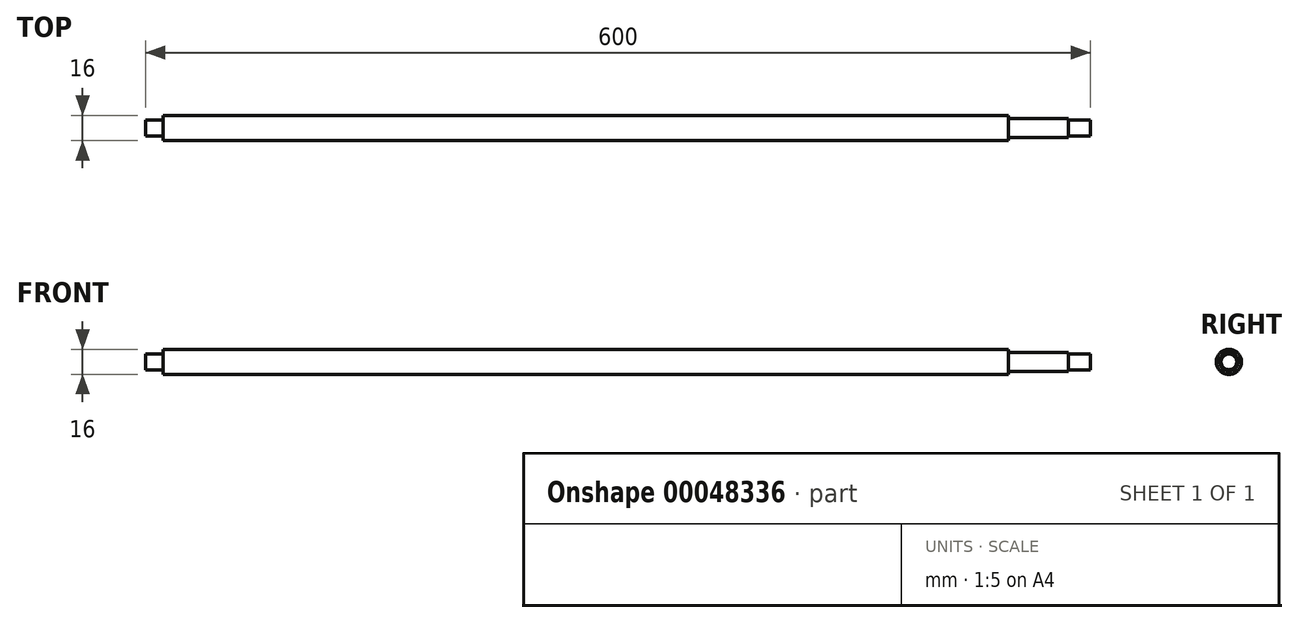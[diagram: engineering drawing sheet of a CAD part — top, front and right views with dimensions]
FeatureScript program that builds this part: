
annotation { "Feature Type Name" : "Feature", "Feature Type Description" : "" }
export const myFeature = defineFeature(function(context is Context, id is Id, definition is map)
    precondition{}
    {
        {
            var Q0;
            Q0=qCreatedBy(makeId("Top.planeOp"),FACE);
            var sketch = newSketch(context, id + "F0", { "sketchPlane" : qUnion([Q0])});
            skLineSegment(sketch, "E0", {"start": v(-350.57, -40.96) * mm, "end": v(249.43, -40.96) * mm});
            skLineSegment(sketch, "E1", {"start": v(-350.57, -40.96) * mm, "end": v(-350.57, -35.96) * mm});
            skLineSegment(sketch, "E2", {"start": v(-350.57, -35.96) * mm, "end": v(-339.57, -35.96) * mm});
            skLineSegment(sketch, "E3", {"start": v(-339.57, -35.96) * mm, "end": v(-339.57, -32.96) * mm});
            skLineSegment(sketch, "E4", {"start": v(-339.57, -32.96) * mm, "end": v(197.43, -32.96) * mm});
            skLineSegment(sketch, "E5", {"start": v(197.43, -32.96) * mm, "end": v(197.43, -34.96) * mm});
            skLineSegment(sketch, "E6", {"start": v(197.43, -34.96) * mm, "end": v(235.43, -34.96) * mm});
            skLineSegment(sketch, "E7", {"start": v(235.43, -34.96) * mm, "end": v(235.43, -35.96) * mm});
            skLineSegment(sketch, "E8", {"start": v(235.43, -35.96) * mm, "end": v(249.43, -35.96) * mm});
            skLineSegment(sketch, "E9", {"start": v(249.43, -35.96) * mm, "end": v(249.43, -40.96) * mm});
            skSolve(sketch);
        }
        {
            var Q0;
            Q0=makeQuery(id+"F0.imprint","IMPRINT",FACE,{"disambiguationData":[TD([[makeQuery(id+"F0.imprint","IMPRINT",EDGE,{"derivedFrom":sQuery(id+"F0.wireOp",EDGE,"E0")}),1.0]])]});
            var Q1;
            Q1=sQuery(id+"F0.wireOp",EDGE,"E0");
            revolve(context, id + "F1", {"entities" : qUnion([Q0]), "axis" : qUnion([Q1]), "revolveType" : RevolveType.FULL});
        }
    });
